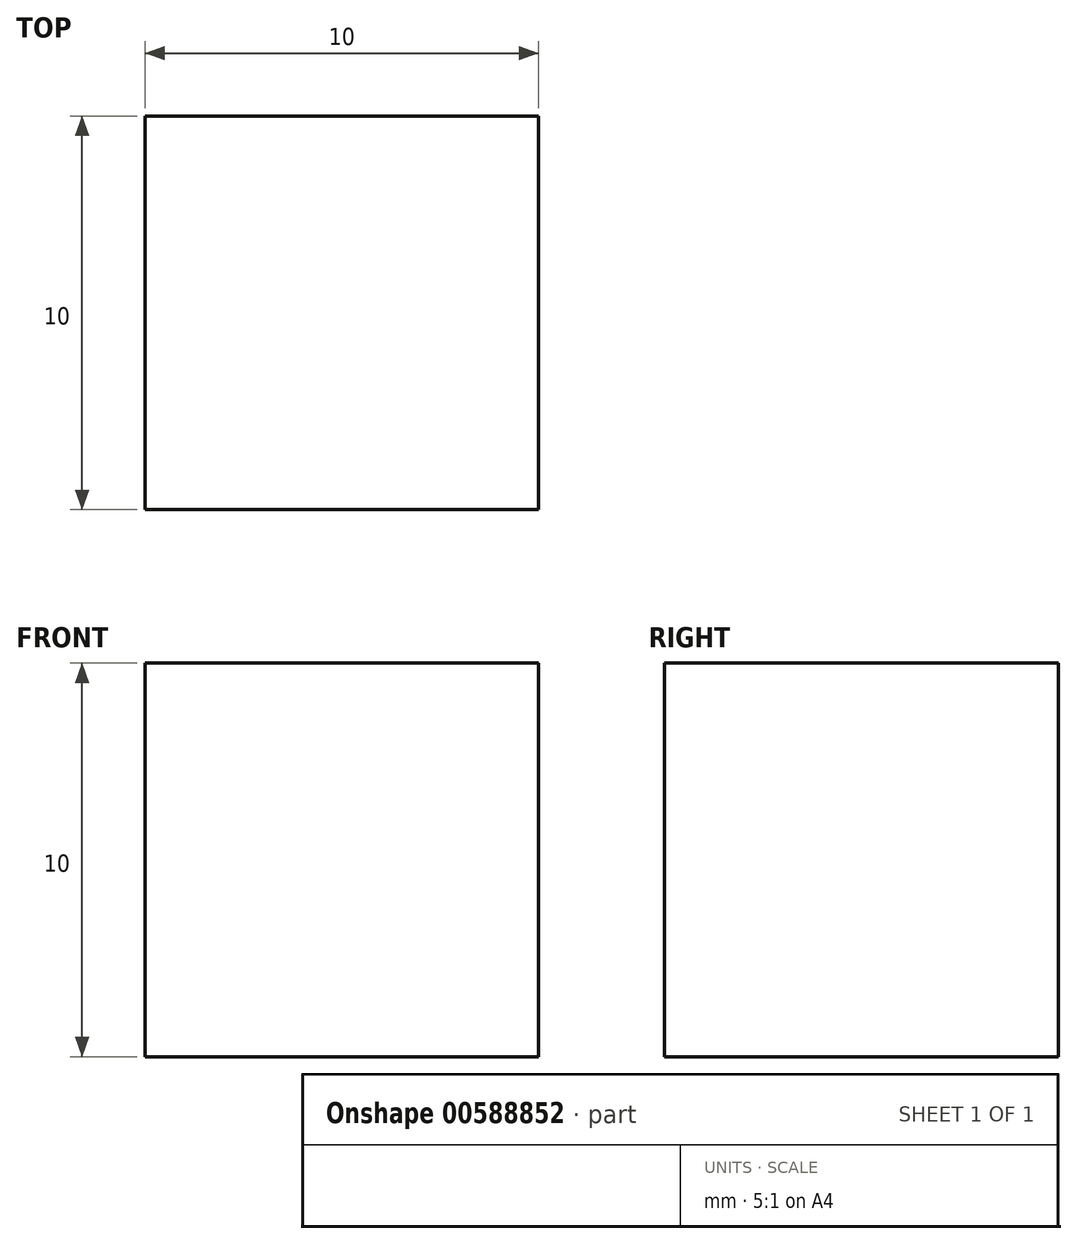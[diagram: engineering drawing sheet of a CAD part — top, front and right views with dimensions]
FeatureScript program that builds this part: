
annotation { "Feature Type Name" : "Feature", "Feature Type Description" : "" }
export const myFeature = defineFeature(function(context is Context, id is Id, definition is map)
    precondition{}
    {
        {
            var Q0;
            Q0=qCreatedBy(makeId("Top.planeOp"),FACE);
            var sketch = newSketch(context, id + "F0", { "sketchPlane" : qUnion([Q0])});
            skLineSegment(sketch, "E0.bottom", {"start": v(0, 0) * mm, "end": v(10, 0) * mm});
            skLineSegment(sketch, "E0.top", {"start": v(0, 10) * mm, "end": v(10, 10) * mm});
            skLineSegment(sketch, "E0.left", {"start": v(0, 0) * mm, "end": v(0, 10) * mm});
            skLineSegment(sketch, "E0.right", {"start": v(10, 0) * mm, "end": v(10, 10) * mm});
            skSolve(sketch);
        }
        {
            var Q0;
            Q0 = qSketchRegion(id + "F0", true);
            extrude(context, id + "F1", {"entities" : qUnion([Q0]), "depth" : 10 * mm, "offsetDistance" : 25 * mm});
        }
    });
